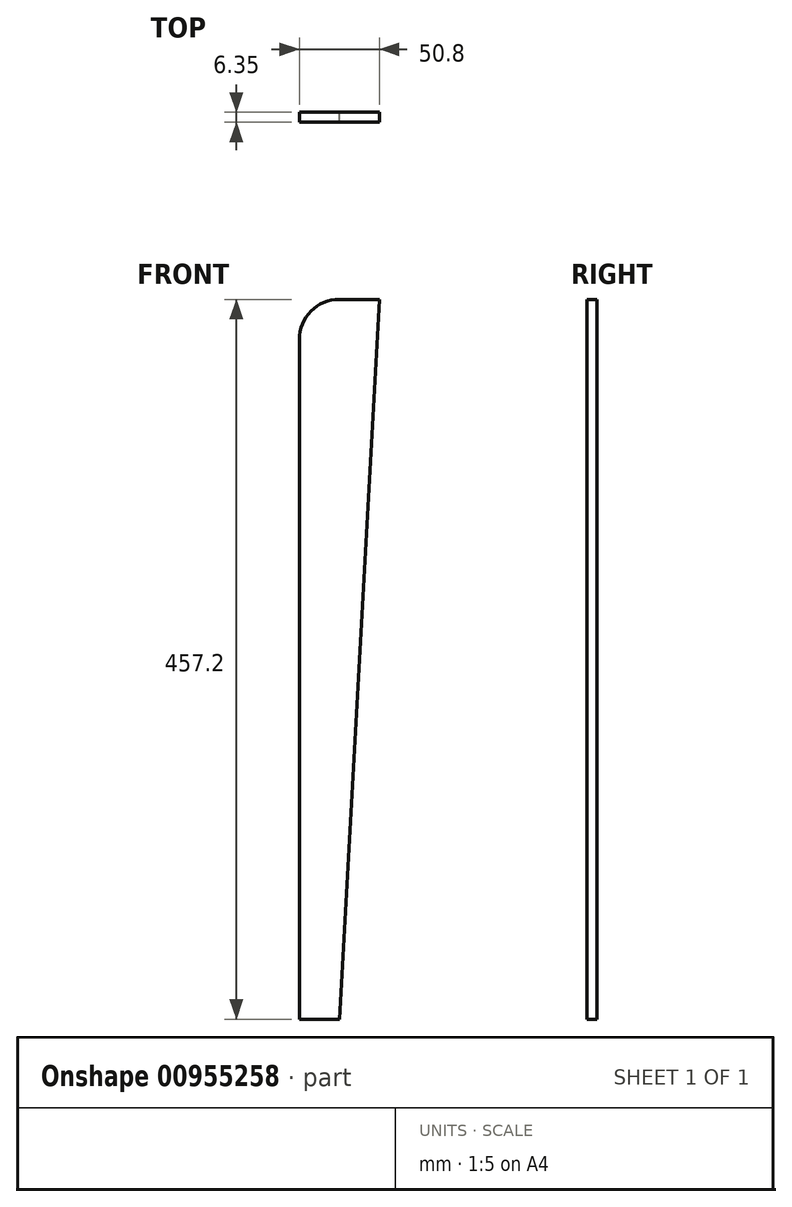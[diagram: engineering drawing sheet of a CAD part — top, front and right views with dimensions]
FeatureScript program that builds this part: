
annotation { "Feature Type Name" : "Feature", "Feature Type Description" : "" }
export const myFeature = defineFeature(function(context is Context, id is Id, definition is map)
    precondition{}
    {
        {
            var Q0;
            Q0=qCreatedBy(makeId("Front.planeOp"),FACE);
            var sketch = newSketch(context, id + "F0", { "sketchPlane" : qUnion([Q0])});
            skLineSegment(sketch, "E0.bottom", {"start": v(0, 0) * mm, "end": v(25.4, 0) * mm});
            skLineSegment(sketch, "E0.top", {"start": v(25.4, 457.2) * mm, "end": v(50.8, 457.2) * mm});
            skLineSegment(sketch, "E0.left", {"start": v(0, 0) * mm, "end": v(0, 431.8) * mm});
            skLineSegment(sketch, "E1", {"start": v(25.4, 0) * mm, "end": v(50.8, 457.2) * mm});
            skPoint(sketch, "E0.right.start.orphan", {"position": v(50.8, 0) * mm});
            skPoint(sketch, "E2.visualSharp", {"position": v(0, 457.2) * mm});
            skArc(sketch, "E2.filletArc", {"start": v(25.4, 457.2) * mm, "mid": v(7.44, 449.76) * mm, "end": v(0, 431.8) * mm});
            skSolve(sketch);
        }
        {
            var Q0;
            Q0=makeQuery(id+"F0.imprint","IMPRINT",FACE,{"disambiguationData":[TD([[makeQuery(id+"F0.imprint","IMPRINT",EDGE,{"derivedFrom":sQuery(id+"F0.wireOp",EDGE,"E0.bottom")}),1.0]])]});
            extrude(context, id + "F1", {"entities" : qUnion([Q0]), "depth" : 6.35 * mm, "offsetDistance" : 25.4 * mm});
        }
    });
